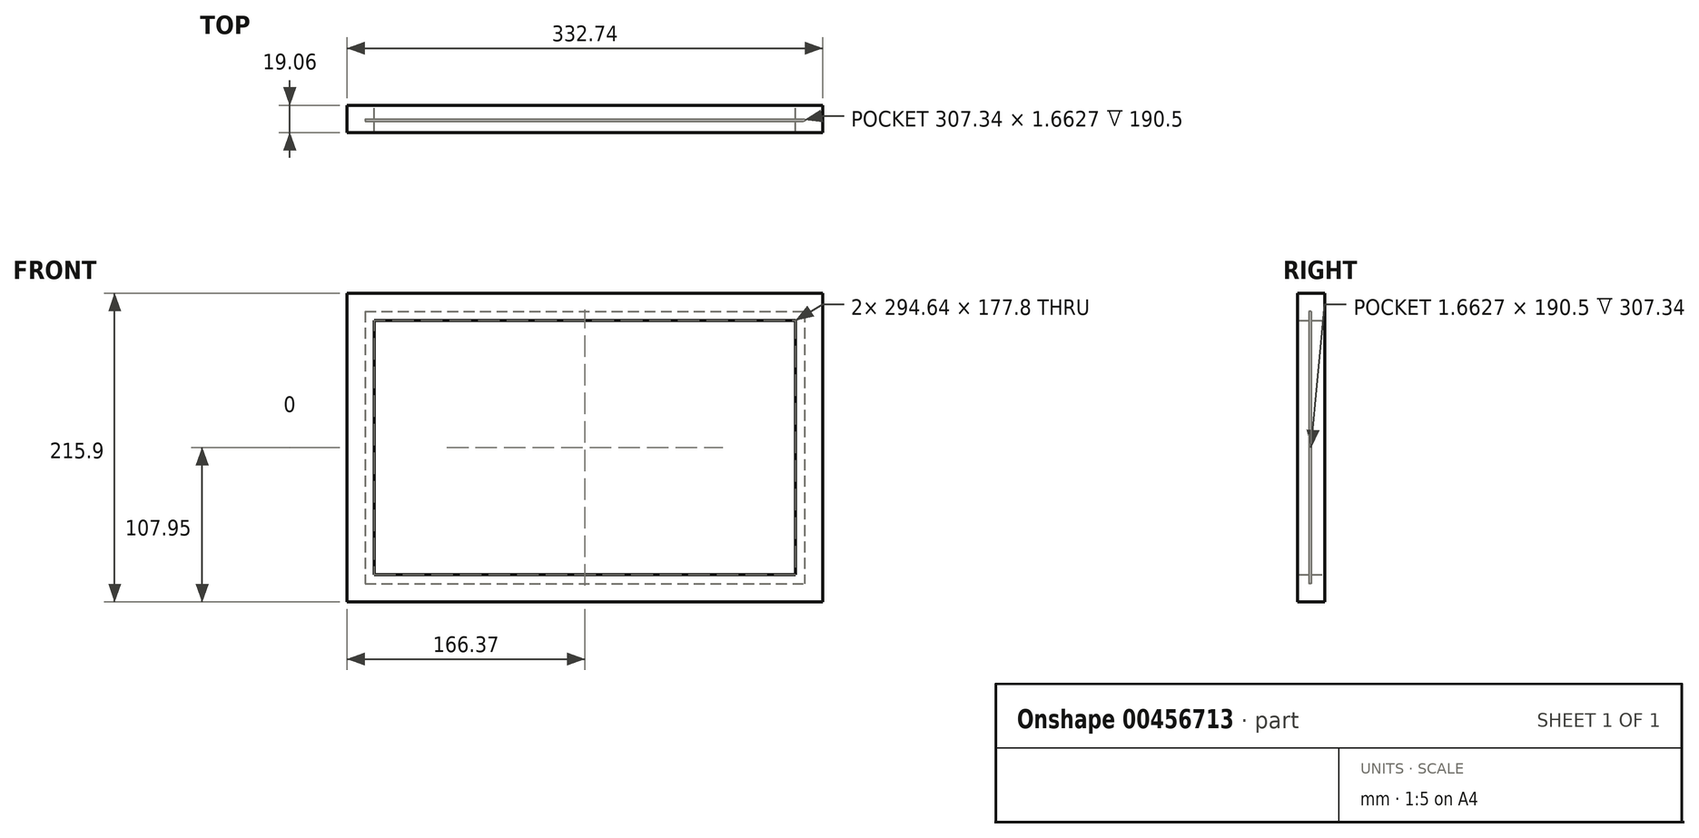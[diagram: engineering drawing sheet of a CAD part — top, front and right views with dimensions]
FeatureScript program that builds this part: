
annotation { "Feature Type Name" : "Feature", "Feature Type Description" : "" }
export const myFeature = defineFeature(function(context is Context, id is Id, definition is map)
    precondition{}
    {
        {
            var Q0;
            Q0=qCreatedBy(makeId("Front.planeOp"),FACE);
            var sketch = newSketch(context, id + "F0", { "sketchPlane" : qUnion([Q0])});
            skLineSegment(sketch, "E0.bottom", {"start": v(-166.37, 107.95) * mm, "end": v(166.37, 107.95) * mm});
            skLineSegment(sketch, "E0.top", {"start": v(-166.37, -107.95) * mm, "end": v(166.37, -107.95) * mm});
            skLineSegment(sketch, "E0.left", {"start": v(-166.37, 107.95) * mm, "end": v(-166.37, -107.95) * mm});
            skLineSegment(sketch, "E0.right", {"start": v(166.37, 107.95) * mm, "end": v(166.37, -107.95) * mm});
            skPoint(sketch, "E0.middle", {"position": v(0, 0) * mm});
            skLineSegment(sketch, "E1.0", {"start": v(-147.32, 88.9) * mm, "end": v(147.32, 88.9) * mm});
            skLineSegment(sketch, "E1.1", {"start": v(-147.32, 88.9) * mm, "end": v(-147.32, -88.9) * mm});
            skLineSegment(sketch, "E1.2", {"start": v(-147.32, -88.9) * mm, "end": v(147.32, -88.9) * mm});
            skLineSegment(sketch, "E1.3", {"start": v(147.32, 88.9) * mm, "end": v(147.32, -88.9) * mm});
            skSolve(sketch);
        }
        {
            var Q0;
            Q0=makeQuery(id+"F0.imprint","IMPRINT",FACE,{"disambiguationData":[TD([[makeQuery(id+"F0.imprint","IMPRINT",EDGE,{"derivedFrom":sQuery(id+"F0.wireOp",EDGE,"E0.bottom")}),-1.0]])]});
            extrude(context, id + "F1", {"entities" : qUnion([Q0]), "depth" : 9.52 * mm, "hasSecondDirection" : true, "secondDirectionOppositeDirection" : true, "secondDirectionDepth" : 9.52 * mm});
        }
        {
            var Q0;
            Q0=qCreatedBy(makeId("Front.planeOp"),FACE);
            var sketch = newSketch(context, id + "F2", { "sketchPlane" : qUnion([Q0])});
            skLineSegment(sketch, "E2.0", {"start": v(-153.67, 95.25) * mm, "end": v(153.67, 95.25) * mm});
            skLineSegment(sketch, "E2.1", {"start": v(-153.67, 95.25) * mm, "end": v(-153.67, -95.25) * mm});
            skLineSegment(sketch, "E2.2", {"start": v(-153.67, -95.25) * mm, "end": v(153.67, -95.25) * mm});
            skLineSegment(sketch, "E2.3", {"start": v(153.67, 95.25) * mm, "end": v(153.67, -95.25) * mm});
            skSolve(sketch);
        }
        {
            var Q0;
            Q0 = qSketchRegion(id + "F2", true);
            extrude(context, id + "F3", {"entities" : qUnion([Q0]), "operationType" : NewBodyOperationType.REMOVE, "oppositeDirection" : true, "depth" : ((1 / 8) / 2) * mm, "hasSecondDirection" : true, "secondDirectionOppositeDirection" : false, "secondDirectionDepth" : 1.6 * mm});
        }
    });
